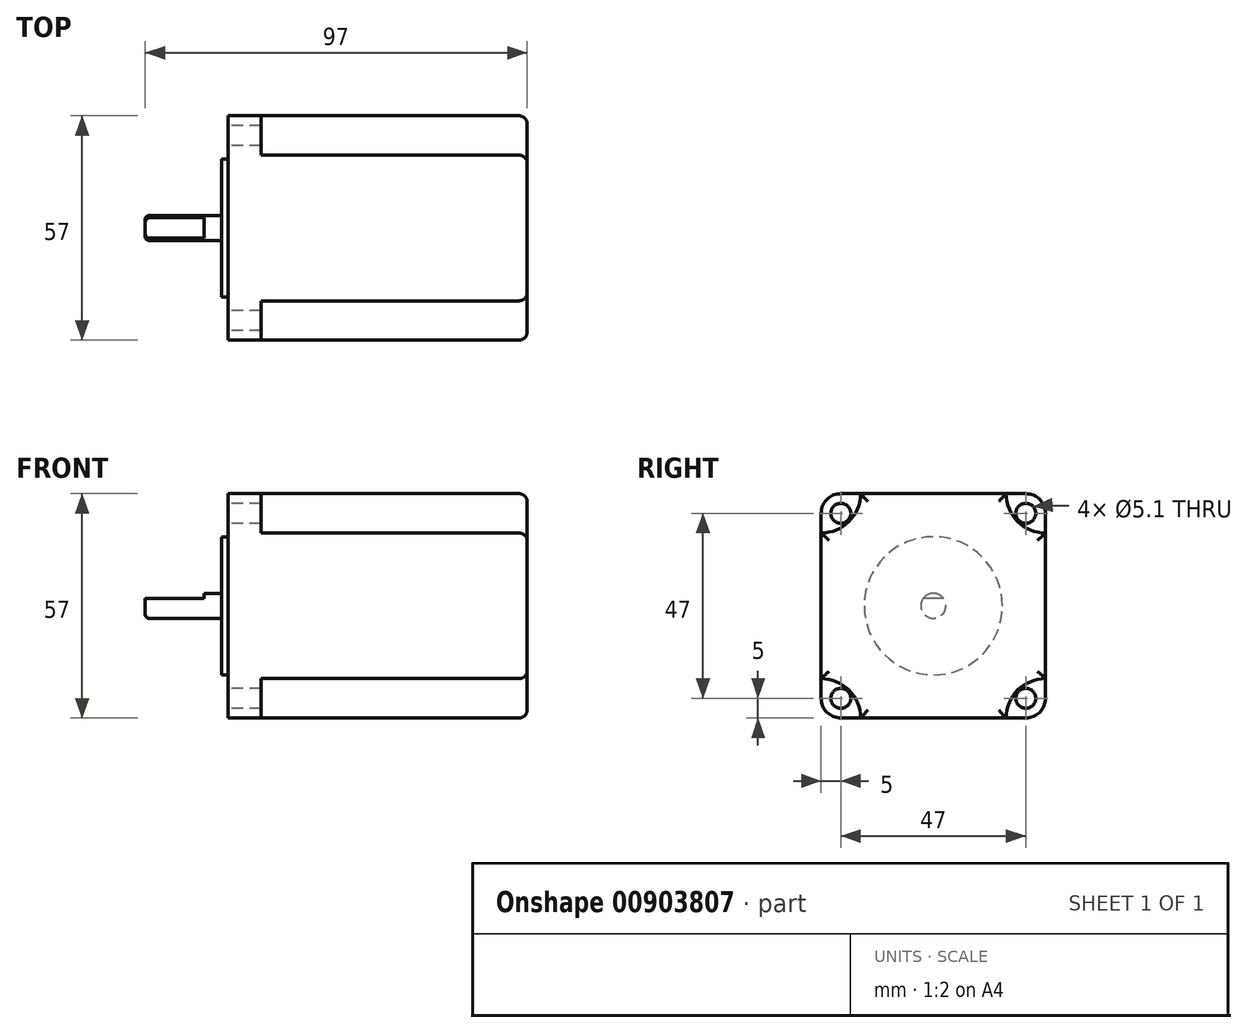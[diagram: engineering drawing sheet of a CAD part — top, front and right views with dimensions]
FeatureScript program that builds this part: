
annotation { "Feature Type Name" : "Feature", "Feature Type Description" : "" }
export const myFeature = defineFeature(function(context is Context, id is Id, definition is map)
    precondition{}
    {
        {
            var Q0;
            Q0=qCreatedBy(makeId("Top.planeOp"),FACE);
            var sketch = newSketch(context, id + "F0", { "sketchPlane" : qUnion([Q0])});
            skLineSegment(sketch, "E0.bottom", {"start": v(38, -28.5) * mm, "end": v(-38, -28.5) * mm});
            skLineSegment(sketch, "E0.top", {"start": v(38, 28.5) * mm, "end": v(-38, 28.5) * mm});
            skLineSegment(sketch, "E0.left", {"start": v(38, -28.5) * mm, "end": v(38, 28.5) * mm});
            skLineSegment(sketch, "E0.right", {"start": v(-38, -28.5) * mm, "end": v(-38, 28.5) * mm});
            skPoint(sketch, "E0.middle", {"position": v(0, 0) * mm});
            skSolve(sketch);
        }
        {
            var Q0;
            Q0=qSketchRegion(id+"F0",true);
            extrude(context, id + "F1", {"entities" : qUnion([Q0]), "depth" : 57 * mm, "offsetDistance" : 25 * mm});
        }
        {
            var Q0;
            Q0=makeQuery(id+"F1.opExtrude","SWEPT_FACE",FACE,{"disambiguationData":[OSD([sQuery(id+"F0.wireOp",EDGE,"E0.right")])]});
            var sketch = newSketch(context, id + "F2", { "sketchPlane" : qUnion([Q0])});
            skCircle(sketch, "E1", {"center": v(0, 28.5) * mm, "radius": 17.55 * mm});
            skLineSegment(sketch, "E2", {"start": v(0, 28.5) * mm, "end": v(0, 57) * mm, "construction": true});
            skLineSegment(sketch, "E3", {"start": v(0, 0) * mm, "end": v(0, 28.5) * mm, "construction": true});
            skSolve(sketch);
        }
        {
            var Q0;
            Q0=qSketchRegion(id+"F2",true);
            extrude(context, id + "F3", {"entities" : qUnion([Q0]), "operationType" : NewBodyOperationType.ADD, "depth" : 1.6 * mm, "offsetDistance" : 25 * mm});
        }
        {
            var Q0;
            Q0=makeQuery(id+"F1.opExtrude","SWEPT_FACE",FACE,{"disambiguationData":[OSD([sQuery(id+"F0.wireOp",EDGE,"E0.right")])]});
            var sketch = newSketch(context, id + "F4", { "sketchPlane" : qUnion([Q0])});
            skLineSegment(sketch, "E4.bottom", {"start": v(-23.5, 52) * mm, "end": v(23.5, 52) * mm, "construction": true});
            skLineSegment(sketch, "E4.top", {"start": v(-23.5, 5) * mm, "end": v(23.5, 5) * mm, "construction": true});
            skLineSegment(sketch, "E4.left", {"start": v(-23.5, 52) * mm, "end": v(-23.5, 5) * mm, "construction": true});
            skLineSegment(sketch, "E4.right", {"start": v(23.5, 52) * mm, "end": v(23.5, 5) * mm, "construction": true});
            skLineSegment(sketch, "E5", {"start": v(-23.5, 57) * mm, "end": v(-23.5, 52) * mm, "construction": true});
            skLineSegment(sketch, "E6", {"start": v(-23.5, 5) * mm, "end": v(-23.5, 0) * mm, "construction": true});
            skLineSegment(sketch, "E7", {"start": v(-23.5, 5) * mm, "end": v(-28.5, 5) * mm, "construction": true});
            skLineSegment(sketch, "E8", {"start": v(23.5, 5) * mm, "end": v(28.5, 5) * mm, "construction": true});
            skCircle(sketch, "E9", {"center": v(-23.5, 52) * mm, "radius": 2.55 * mm});
            skCircle(sketch, "E10", {"center": v(23.5, 52) * mm, "radius": 2.55 * mm});
            skCircle(sketch, "E11", {"center": v(-23.5, 5) * mm, "radius": 2.55 * mm});
            skCircle(sketch, "E12", {"center": v(23.5, 5) * mm, "radius": 2.55 * mm});
            skSolve(sketch);
        }
        {
            var Q0;
            Q0=makeQuery(id+"F4.imprint","IMPRINT",FACE,{"disambiguationData":[TD([[makeQuery(id+"F4.imprint","IMPRINT",EDGE,{"derivedFrom":sQuery(id+"F4.wireOp",EDGE,"E9")}),1.0]])]});
            var Q1;
            Q1=makeQuery(id+"F4.imprint","IMPRINT",FACE,{"disambiguationData":[TD([[makeQuery(id+"F4.imprint","IMPRINT",EDGE,{"derivedFrom":sQuery(id+"F4.wireOp",EDGE,"E10")}),1.0]])]});
            var Q2;
            Q2=makeQuery(id+"F4.imprint","IMPRINT",FACE,{"disambiguationData":[TD([[makeQuery(id+"F4.imprint","IMPRINT",EDGE,{"derivedFrom":sQuery(id+"F4.wireOp",EDGE,"E12")}),1.0]])]});
            var Q3;
            Q3=makeQuery(id+"F4.imprint","IMPRINT",FACE,{"disambiguationData":[TD([[makeQuery(id+"F4.imprint","IMPRINT",EDGE,{"derivedFrom":sQuery(id+"F4.wireOp",EDGE,"E11")}),1.0]])]});
            var Q4;
            Q4=sQuery(id+"F4.wireOp",EDGE,"E4.left");
            var Q5;
            Q5=sQuery(id+"F4.wireOp",EDGE,"E4.bottom");
            var Q6;
            Q6=sQuery(id+"F4.wireOp",EDGE,"E4.right");
            var Q7;
            Q7=sQuery(id+"F4.wireOp",EDGE,"E4.top");
            extrude(context, id + "F5", {"entities" : qUnion([Q0, Q1, Q2, Q3]), "operationType" : NewBodyOperationType.REMOVE, "surfaceEntities" : qUnion([Q4, Q5, Q6, Q7]), "oppositeDirection" : true, "depth" : 25 * mm, "offsetDistance" : 25 * mm});
        }
        {
            var Q0;
            Q0=makeQuery(id+"F1.opExtrude","SWEPT_FACE",FACE,{"disambiguationData":[OSD([sQuery(id+"F0.wireOp",EDGE,"E0.left")])]});
            var sketch = newSketch(context, id + "F6", { "sketchPlane" : qUnion([Q0])});
            skArc(sketch, "E13", {"start": v(-28.5, 47) * mm, "mid": v(-21.43, 49.93) * mm, "end": v(-18.5, 57) * mm});
            skArc(sketch, "E14", {"start": v(-18.5, 0) * mm, "mid": v(-21.43, 7.07) * mm, "end": v(-28.5, 10) * mm});
            skArc(sketch, "E15", {"start": v(28.5, 10) * mm, "mid": v(21.43, 7.07) * mm, "end": v(18.5, 0) * mm});
            skPoint(sketch, "E16.end.orphan", {"position": v(28.5, 47) * mm});
            skPoint(sketch, "E16.start.orphan", {"position": v(18.5, 57) * mm});
            skArc(sketch, "E17", {"start": v(18.5, 57) * mm, "mid": v(21.43, 49.93) * mm, "end": v(28.5, 47) * mm});
            skLineSegment(sketch, "E18", {"start": v(-28.5, 47) * mm, "end": v(-28.5, 57) * mm});
            skLineSegment(sketch, "E19", {"start": v(-18.5, 57) * mm, "end": v(-28.5, 57) * mm});
            skLineSegment(sketch, "E20", {"start": v(18.5, 57) * mm, "end": v(28.5, 57) * mm});
            skLineSegment(sketch, "E21", {"start": v(28.5, 47) * mm, "end": v(28.5, 57) * mm});
            skLineSegment(sketch, "E22", {"start": v(28.5, 0) * mm, "end": v(28.5, 10) * mm});
            skLineSegment(sketch, "E23", {"start": v(28.5, 0) * mm, "end": v(18.5, 0) * mm});
            skLineSegment(sketch, "E24", {"start": v(-18.5, 0) * mm, "end": v(-28.5, 0) * mm});
            skLineSegment(sketch, "E25", {"start": v(-28.5, 10) * mm, "end": v(-28.5, 0) * mm});
            skSolve(sketch);
        }
        {
            var Q0;
            Q0=qSketchRegion(id+"F6",true);
            extrude(context, id + "F7", {"entities" : qUnion([Q0]), "operationType" : NewBodyOperationType.REMOVE, "oppositeDirection" : true, "depth" : 67.5 * mm, "offsetDistance" : 25 * mm});
        }
        {
            var Q0;
            Q0=makeQuery(id+"F1.opExtrude","CAP_EDGE",EDGE,{"disambiguationData":[OSD([sQuery(id+"F0.wireOp",EDGE,"E0.bottom")])],"isStart":false});
            var Q1;
            Q1=makeQuery(id+"F1.opExtrude","CAP_EDGE",EDGE,{"disambiguationData":[OSD([sQuery(id+"F0.wireOp",EDGE,"E0.top")])],"isStart":false});
            var Q2;
            Q2=makeQuery(id+"F1.opExtrude","CAP_EDGE",EDGE,{"disambiguationData":[OSD([sQuery(id+"F0.wireOp",EDGE,"E0.top")])],"isStart":true});
            var Q3;
            Q3=makeQuery(id+"F1.opExtrude","CAP_EDGE",EDGE,{"disambiguationData":[OSD([sQuery(id+"F0.wireOp",EDGE,"E0.bottom")])],"isStart":true});
            fillet(context, id + "F8", {"entities" : qUnion([Q0, Q1, Q2, Q3]), "radius" : 5 * mm, "tangentPropagation" : true, "allowEdgeOverflow" : false});
        }
        {
            var Q0;
            Q0=makeQuery(id+"F7.boolean.opBoolean","COPY",EDGE,{"derivedFrom":makeQuery(id+"F7.opExtrude","SWEPT_EDGE",EDGE,{"disambiguationData":[OSD([sQuery(id+"F0.wireOp",EDGE,"E0.left"),sQuery(id+"F6.wireOp",EDGE,"E13"),sQuery(id+"F6.wireOp",EDGE,"E19")])]})});
            var Q1;
            Q1=makeQuery(id+"F7.boolean.opBoolean","COPY",EDGE,{"derivedFrom":makeQuery(id+"F7.opExtrude","SWEPT_EDGE",EDGE,{"disambiguationData":[OSD([sQuery(id+"F0.wireOp",EDGE,"E0.bottom"),sQuery(id+"F0.wireOp",EDGE,"E0.left"),sQuery(id+"F6.wireOp",EDGE,"E13"),sQuery(id+"F6.wireOp",EDGE,"E18")])]})});
            var Q2;
            Q2=makeQuery(id+"F7.boolean.opBoolean","COPY",EDGE,{"derivedFrom":makeQuery(id+"F7.opExtrude","SWEPT_EDGE",EDGE,{"disambiguationData":[OSD([sQuery(id+"F0.wireOp",EDGE,"E0.bottom"),sQuery(id+"F0.wireOp",EDGE,"E0.left"),sQuery(id+"F6.wireOp",EDGE,"E14"),sQuery(id+"F6.wireOp",EDGE,"E25")])]})});
            var Q3;
            Q3=makeQuery(id+"F7.boolean.opBoolean","COPY",EDGE,{"derivedFrom":makeQuery(id+"F7.opExtrude","SWEPT_EDGE",EDGE,{"disambiguationData":[OSD([sQuery(id+"F0.wireOp",EDGE,"E0.left"),sQuery(id+"F6.wireOp",EDGE,"E14"),sQuery(id+"F6.wireOp",EDGE,"E24")])]})});
            var Q4;
            Q4=makeQuery(id+"F7.boolean.opBoolean","COPY",EDGE,{"derivedFrom":makeQuery(id+"F7.opExtrude","SWEPT_EDGE",EDGE,{"disambiguationData":[OSD([sQuery(id+"F0.wireOp",EDGE,"E0.left"),sQuery(id+"F6.wireOp",EDGE,"E17"),sQuery(id+"F6.wireOp",EDGE,"E20")])]})});
            var Q5;
            Q5=makeQuery(id+"F7.boolean.opBoolean","COPY",EDGE,{"derivedFrom":makeQuery(id+"F7.opExtrude","SWEPT_EDGE",EDGE,{"disambiguationData":[OSD([sQuery(id+"F0.wireOp",EDGE,"E0.top"),sQuery(id+"F0.wireOp",EDGE,"E0.left"),sQuery(id+"F6.wireOp",EDGE,"E17"),sQuery(id+"F6.wireOp",EDGE,"E21")])]})});
            var Q6;
            Q6=makeQuery(id+"F7.boolean.opBoolean","COPY",EDGE,{"derivedFrom":makeQuery(id+"F7.opExtrude","SWEPT_EDGE",EDGE,{"disambiguationData":[OSD([sQuery(id+"F0.wireOp",EDGE,"E0.top"),sQuery(id+"F0.wireOp",EDGE,"E0.left"),sQuery(id+"F6.wireOp",EDGE,"E15"),sQuery(id+"F6.wireOp",EDGE,"E22")])]})});
            var Q7;
            Q7=makeQuery(id+"F7.boolean.opBoolean","COPY",EDGE,{"derivedFrom":makeQuery(id+"F7.opExtrude","SWEPT_EDGE",EDGE,{"disambiguationData":[OSD([sQuery(id+"F0.wireOp",EDGE,"E0.left"),sQuery(id+"F6.wireOp",EDGE,"E15"),sQuery(id+"F6.wireOp",EDGE,"E23")])]})});
            var Q8;
            Q8=makeQuery(id+"F1.opExtrude","SWEPT_FACE",FACE,{"disambiguationData":[OSD([sQuery(id+"F0.wireOp",EDGE,"E0.left")])]});
            var Q9;
            Q9=makeQuery(id+"F1.opExtrude","SWEPT_EDGE",EDGE,{"disambiguationData":[OSD([sQuery(id+"F0.wireOp",EDGE,"E0.top"),sQuery(id+"F0.wireOp",EDGE,"E0.left")])]});
            fillet(context, id + "F9", {"entities" : qUnion([Q0, Q1, Q2, Q3, Q4, Q5, Q6, Q7, Q8, Q9]), "radius" : 2 * mm, "tangentPropagation" : true, "allowEdgeOverflow" : false});
        }
        {
            var Q0;
            Q0=makeQuery(id+"F3.opExtrude","CAP_FACE",FACE,{"disambiguationData":[OSD([sQuery(id+"F2.wireOp",EDGE,"E1")])],"isStart":false});
            var sketch = newSketch(context, id + "F10", { "sketchPlane" : qUnion([Q0])});
            skCircle(sketch, "E26", {"center": v(0, 28.5) * mm, "radius": 3.18 * mm});
            skSolve(sketch);
        }
        {
            var Q0;
            Q0=qSketchRegion(id+"F10",true);
            extrude(context, id + "F11", {"entities" : qUnion([Q0]), "depth" : 19.4 * mm, "offsetDistance" : 25 * mm});
        }
        {
            var Q0;
            Q0=makeQuery(id+"F11.opExtrude","CAP_FACE",FACE,{"disambiguationData":[OSD([sQuery(id+"F10.wireOp",EDGE,"E26")])],"isStart":false});
            var sketch = newSketch(context, id + "F12", { "sketchPlane" : qUnion([Q0])});
            skLineSegment(sketch, "E27", {"start": v(-2.6, 30.33) * mm, "end": v(2.6, 30.33) * mm});
            skPoint(sketch, "E28", {"position": v(0, 31.68) * mm});
            skArc(sketch, "E29", {"start": v(2.6, 30.33) * mm, "mid": v(0, 31.68) * mm, "end": v(-2.6, 30.33) * mm});
            skSolve(sketch);
        }
        {
            var Q0;
            Q0=qSketchRegion(id+"F12",true);
            extrude(context, id + "F13", {"entities" : qUnion([Q0]), "operationType" : NewBodyOperationType.REMOVE, "oppositeDirection" : true, "depth" : 15 * mm, "offsetDistance" : 25 * mm});
        }
        {
            var Q0;
            Q0=makeQuery(id+"F11.opExtrude","CAP_EDGE",EDGE,{"disambiguationData":[OSD([sQuery(id+"F10.wireOp",EDGE,"E26")])],"isStart":false});
            fillet(context, id + "F14", {"entities" : qUnion([Q0]), "radius" : 1 * mm, "tangentPropagation" : true, "allowEdgeOverflow" : false});
        }
    });
